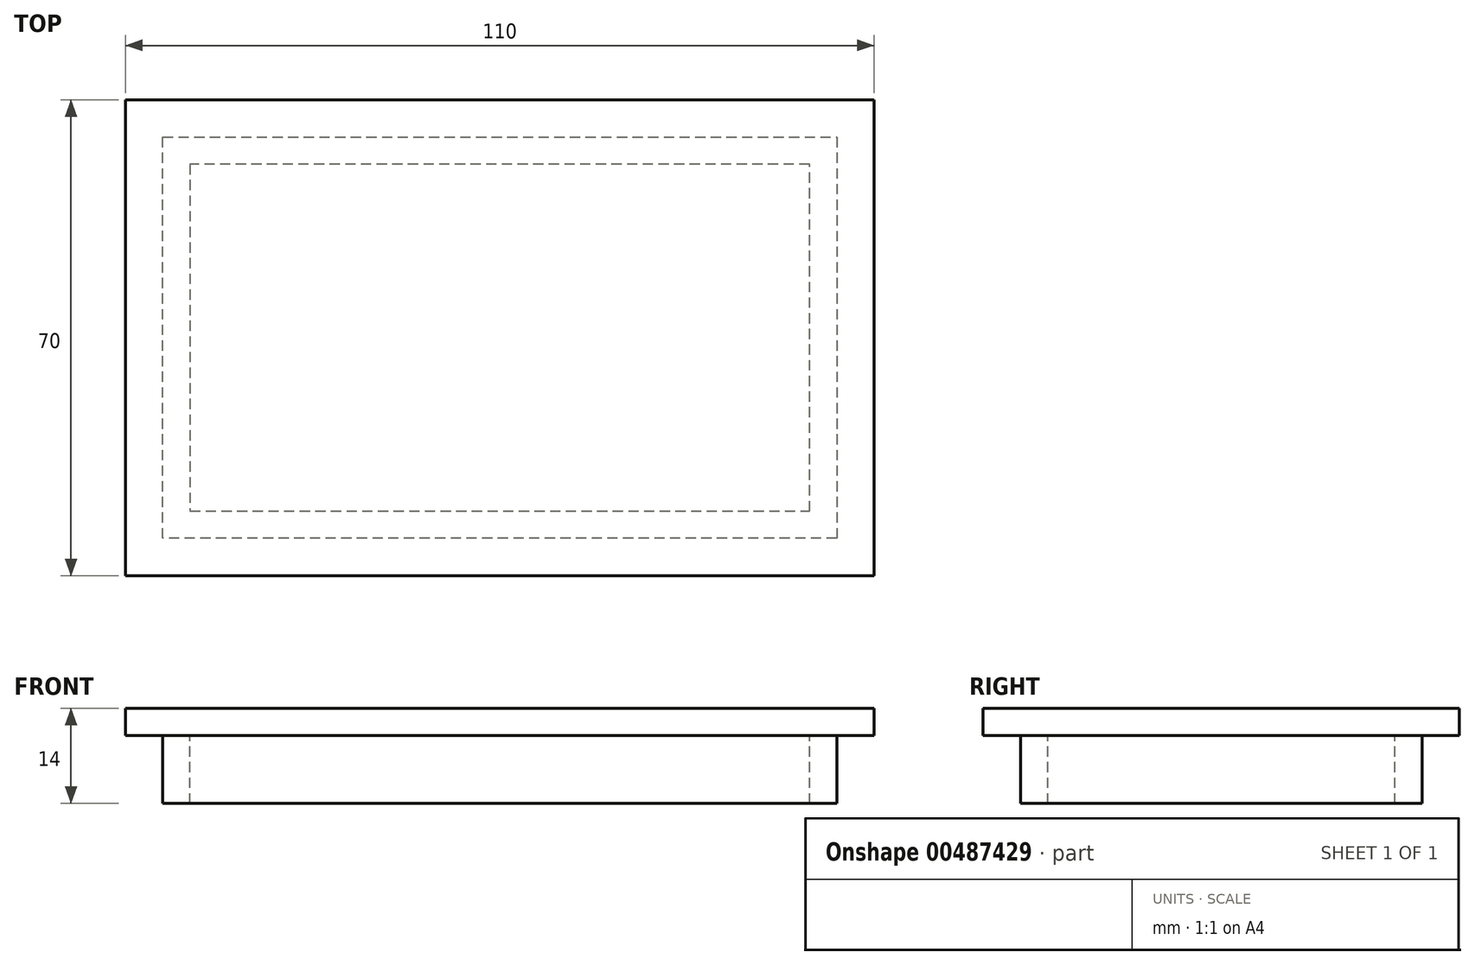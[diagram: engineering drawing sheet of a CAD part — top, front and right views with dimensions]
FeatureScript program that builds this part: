
annotation { "Feature Type Name" : "Feature", "Feature Type Description" : "" }
export const myFeature = defineFeature(function(context is Context, id is Id, definition is map)
    precondition{}
    {
        {
            var Q0;
            Q0=qCreatedBy(makeId("Top.planeOp"),FACE);
            var sketch = newSketch(context, id + "F0", { "sketchPlane" : qUnion([Q0])});
            skLineSegment(sketch, "E0.bottom", {"start": v(-67.32, 0) * mm, "end": v(42.68, 0) * mm});
            skLineSegment(sketch, "E0.top", {"start": v(-67.32, -70) * mm, "end": v(42.68, -70) * mm});
            skLineSegment(sketch, "E0.left", {"start": v(-67.32, 0) * mm, "end": v(-67.32, -70) * mm});
            skLineSegment(sketch, "E0.right", {"start": v(42.68, 0) * mm, "end": v(42.68, -70) * mm});
            skSolve(sketch);
        }
        {
            var Q0;
            Q0=makeQuery(id+"F0.imprint","IMPRINT",FACE,{"disambiguationData":[TD([[makeQuery(id+"F0.imprint","IMPRINT",EDGE,{"derivedFrom":sQuery(id+"F0.wireOp",EDGE,"E0.bottom")}),-1.0]])]});
            extrude(context, id + "F1", {"entities" : qUnion([Q0]), "depth" : 4 * mm});
        }
        {
            var Q0;
            Q0=makeQuery(id+"F1.opExtrude","CAP_FACE",FACE,{"disambiguationData":[OSD([sQuery(id+"F0.wireOp",EDGE,"E0.bottom"),sQuery(id+"F0.wireOp",EDGE,"E0.top"),sQuery(id+"F0.wireOp",EDGE,"E0.left"),sQuery(id+"F0.wireOp",EDGE,"E0.right")])],"isStart":true});
            var sketch = newSketch(context, id + "F2", { "sketchPlane" : qUnion([Q0])});
            skLineSegment(sketch, "E1", {"start": v(-67.32, 35) * mm, "end": v(68.3, 35) * mm, "construction": true});
            skLineSegment(sketch, "E2", {"start": v(-61.82, 72.67) * mm, "end": v(-61.82, -2.53) * mm, "construction": true});
            skPoint(sketch, "E3.startSnap0", {"position": v(-12.32, 70) * mm});
            skLineSegment(sketch, "E4.MirrorCS", {"start": v(-57.82, 72.67) * mm, "end": v(-57.82, -2.53) * mm, "construction": true});
            skLineSegment(sketch, "E5.MirrorCS", {"start": v(37.18, 72.67) * mm, "end": v(37.18, -2.53) * mm, "construction": true});
            skLineSegment(sketch, "E6.MirrorCS", {"start": v(33.18, 72.67) * mm, "end": v(33.18, -2.53) * mm, "construction": true});
            skLineSegment(sketch, "E7", {"start": v(-77.2, 35) * mm, "end": v(56.08, 35) * mm, "construction": true});
            skLineSegment(sketch, "E8", {"start": v(-70.05, 64.5) * mm, "end": v(46.4, 64.5) * mm, "construction": true});
            skLineSegment(sketch, "E9.MirrorCS", {"start": v(-70.05, 60.5) * mm, "end": v(46.4, 60.5) * mm, "construction": true});
            skLineSegment(sketch, "E10.MirrorCS", {"start": v(-70.05, 9.5) * mm, "end": v(46.4, 9.5) * mm, "construction": true});
            skLineSegment(sketch, "E11.MirrorCS", {"start": v(-70.05, 5.5) * mm, "end": v(46.4, 5.5) * mm, "construction": true});
            skLineSegment(sketch, "E12", {"start": v(-61.82, 64.5) * mm, "end": v(-61.82, 5.5) * mm});
            skLineSegment(sketch, "E13", {"start": v(-61.82, 5.5) * mm, "end": v(37.18, 5.5) * mm});
            skLineSegment(sketch, "E14", {"start": v(37.18, 5.5) * mm, "end": v(37.18, 64.5) * mm});
            skLineSegment(sketch, "E15", {"start": v(37.18, 64.5) * mm, "end": v(-61.82, 64.5) * mm});
            skLineSegment(sketch, "E16", {"start": v(-57.82, 60.5) * mm, "end": v(33.18, 60.5) * mm});
            skLineSegment(sketch, "E17", {"start": v(33.18, 60.5) * mm, "end": v(33.18, 9.5) * mm});
            skLineSegment(sketch, "E18", {"start": v(33.18, 9.5) * mm, "end": v(-57.82, 9.5) * mm});
            skLineSegment(sketch, "E19", {"start": v(-57.82, 9.5) * mm, "end": v(-57.82, 60.5) * mm});
            skSolve(sketch);
        }
        {
            var Q0;
            Q0=makeQuery(id+"F2.imprint","IMPRINT",FACE,{"disambiguationData":[TD([[makeQuery(id+"F2.imprint","IMPRINT",EDGE,{"derivedFrom":sQuery(id+"F2.wireOp",EDGE,"E12")}),1.0]])]});
            extrude(context, id + "F3", {"entities" : qUnion([Q0]), "operationType" : NewBodyOperationType.ADD, "depth" : 10 * mm});
        }
    });
